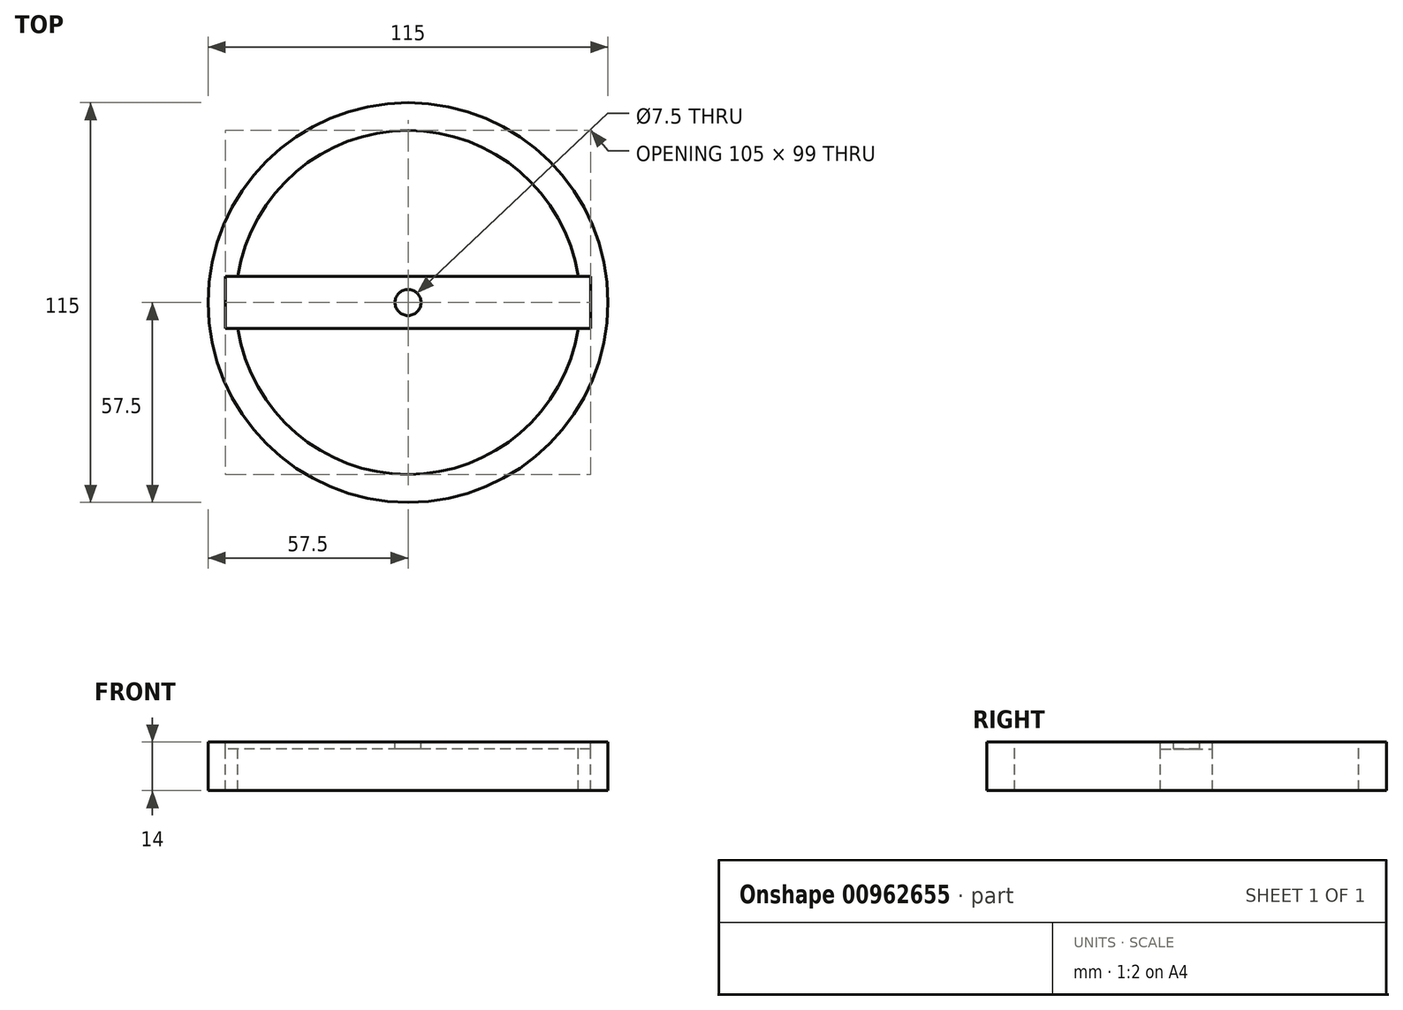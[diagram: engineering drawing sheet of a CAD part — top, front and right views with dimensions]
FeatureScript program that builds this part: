
annotation { "Feature Type Name" : "Feature", "Feature Type Description" : "" }
export const myFeature = defineFeature(function(context is Context, id is Id, definition is map)
    precondition{}
    {
        {
            var Q0;
            Q0=qCreatedBy(makeId("Top.planeOp"),FACE);
            var sketch = newSketch(context, id + "F0", { "sketchPlane" : qUnion([Q0])});
            skCircle(sketch, "E0", {"center": v(0, 0) * mm, "radius": 57.5 * mm});
            skCircle(sketch, "E1", {"center": v(0, 0) * mm, "radius": 49.5 * mm});
            skLineSegment(sketch, "E2.bottom", {"start": v(52.5, -7.5) * mm, "end": v(-52.5, -7.5) * mm});
            skLineSegment(sketch, "E2.top", {"start": v(52.5, 7.5) * mm, "end": v(-52.5, 7.5) * mm});
            skLineSegment(sketch, "E2.left", {"start": v(52.5, -7.5) * mm, "end": v(52.5, 7.5) * mm});
            skLineSegment(sketch, "E2.right", {"start": v(-52.5, -7.5) * mm, "end": v(-52.5, 7.5) * mm});
            skCircle(sketch, "E3", {"center": v(0, 0) * mm, "radius": 3.75 * mm});
            skSolve(sketch);
        }
        {
            var Q0;
            Q0=makeQuery(id+"F0.imprint","IMPRINT",FACE,{"disambiguationData":[TD([[makeQuery(id+"F0.imprint","IMPRINT",EDGE,{"derivedFrom":sQuery(id+"F0.wireOp",EDGE,"E0")}),1.0]])]});
            extrude(context, id + "F1", {"entities" : qUnion([Q0]), "oppositeDirection" : true, "depth" : 14 * mm, "offsetDistance" : 25 * mm});
        }
        {
            var Q0;
            {var subQ5=sQuery(id+"F0.wireOp",EDGE,"E2.right");Q0=makeQuery(id+"F0.imprint","IMPRINT",FACE,{"disambiguationData":[TD([[makeQuery(id+"F0.imprint","IMPRINT",EDGE,{"derivedFrom":subQ5}),-1.0]])]});}
            var Q1;
            Q1=makeQuery(id+"F0.imprint","IMPRINT",FACE,{"disambiguationData":[TD([[makeQuery(id+"F0.imprint","IMPRINT",EDGE,{"derivedFrom":sQuery(id+"F0.wireOp",EDGE,"E3")}),-1.0]])]});
            var Q2;
            {var subQ5=sQuery(id+"F0.wireOp",EDGE,"E2.left");Q2=makeQuery(id+"F0.imprint","IMPRINT",FACE,{"disambiguationData":[TD([[makeQuery(id+"F0.imprint","IMPRINT",EDGE,{"derivedFrom":subQ5}),1.0]])]});}
            extrude(context, id + "F2", {"entities" : qUnion([Q0, Q1, Q2]), "oppositeDirection" : true, "depth" : 2 * mm, "offsetDistance" : 25 * mm});
        }
    });
